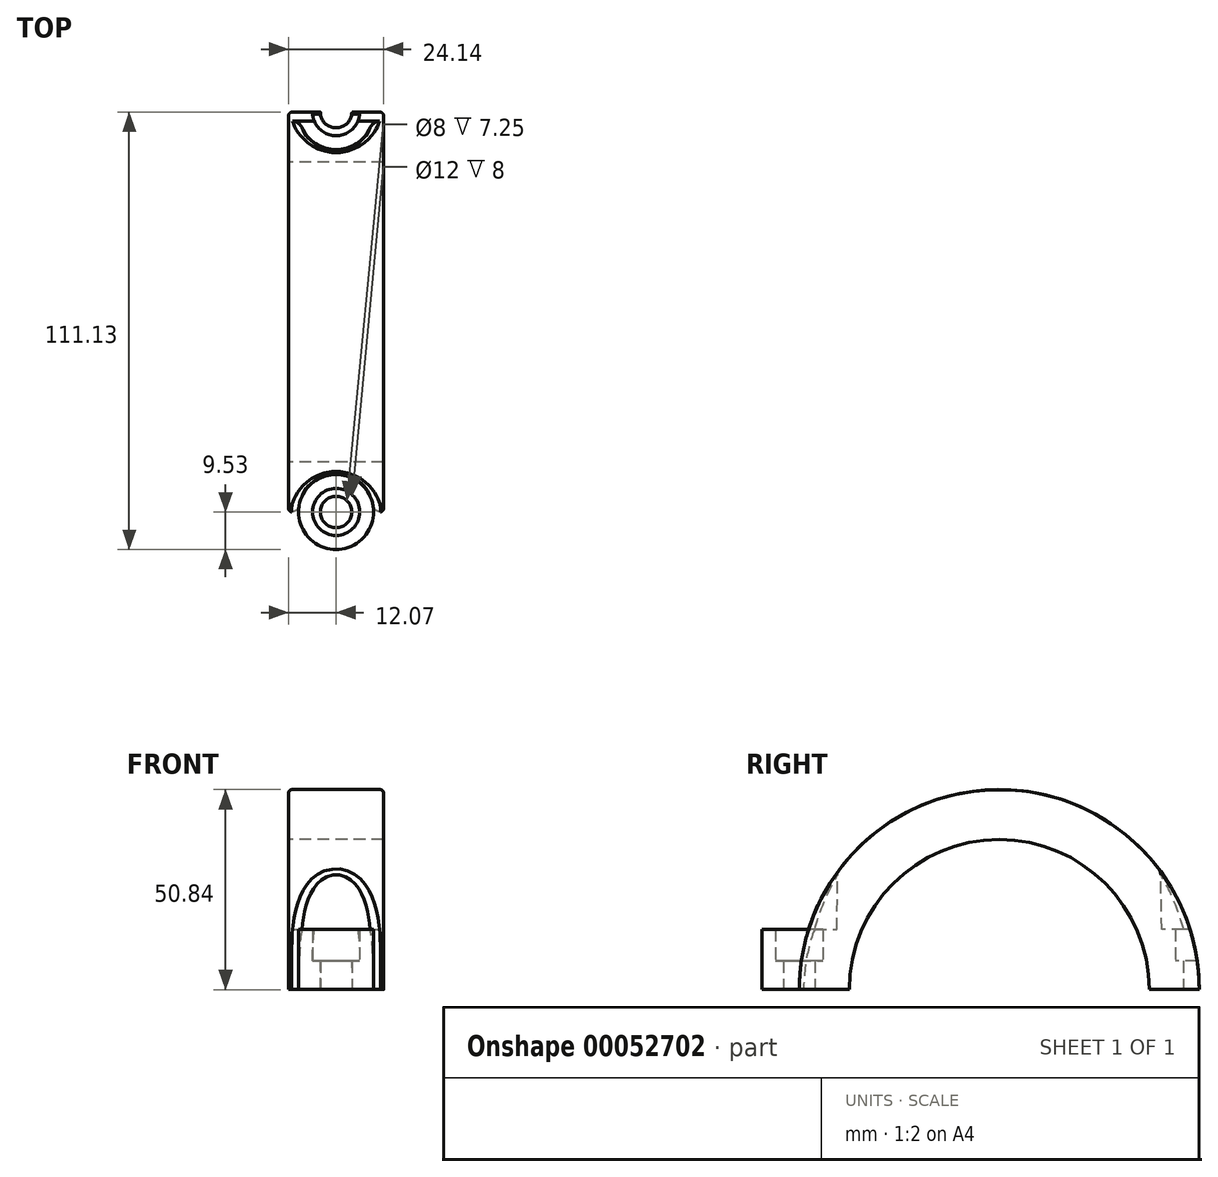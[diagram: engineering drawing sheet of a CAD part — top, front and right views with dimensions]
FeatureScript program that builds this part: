
annotation { "Feature Type Name" : "Feature", "Feature Type Description" : "" }
export const myFeature = defineFeature(function(context is Context, id is Id, definition is map)
    precondition{}
    {
        {
            var Q0;
            Q0=qCreatedBy(makeId("Right.planeOp"),FACE);
            var sketch = newSketch(context, id + "F0", { "sketchPlane" : qUnion([Q0])});
            skArc(sketch, "E0", {"start": v(38.1, 0) * mm, "mid": v(0, 38.1) * mm, "end": v(-38.1, 0) * mm});
            skArc(sketch, "E1.0", {"start": v(50.8, 0) * mm, "mid": v(0, 50.8) * mm, "end": v(-50.8, 0) * mm});
            skLineSegment(sketch, "E2", {"start": v(-50.8, 0) * mm, "end": v(-38.1, 0) * mm});
            skLineSegment(sketch, "E3.trimOffspring", {"start": v(38.1, 0) * mm, "end": v(50.8, 0) * mm});
            skSolve(sketch);
        }
        {
            var Q0;
            Q0 = qSketchRegion(id + "F0", true);
            var Q1;
            Q1=makeQuery(id+"F0.imprint","IMPRINT",FACE,{"disambiguationData":[TD([[makeQuery(id+"F0.imprint","IMPRINT",EDGE,{"derivedFrom":sQuery(id+"F0.wireOp",EDGE,"E0")}),-1.0]])]});
            extrude(context, id + "F1", {"entities" : qUnion([Q0, Q1]), "depth" : 24.13 * mm, "symmetric" : true});
        }
        {
            var Q0;
            Q0=makeQuery(id+"F1.opExtrude","SWEPT_FACE",FACE,{"disambiguationData":[OSD([sQuery(id+"F0.wireOp",EDGE,"E2")])]});
            var sketch = newSketch(context, id + "F2", { "sketchPlane" : qUnion([Q0])});
            skCircle(sketch, "E4", {"center": v(0, 50.8) * mm, "radius": 9.53 * mm});
            skCircle(sketch, "E5.MirrorC", {"center": v(0, -50.8) * mm, "radius": 9.53 * mm});
            skSolve(sketch);
        }
        {
            var Q0;
            {var subQ0=sQuery(id+"F2.wireOp",EDGE,"E4");var subQ1=makeQuery(id+"F1.opExtrude","SWEPT_EDGE",EDGE,{"disambiguationData":[OSD([sQuery(id+"F0.wireOp",EDGE,"E1.0"),sQuery(id+"F0.wireOp",EDGE,"E2")])]});var subQ2=makeQuery(id+"F2.imprint","INTERSECT",VERTEX,{"disambiguationData":[OD(0.0)],"derivedFrom":[subQ1,subQ0]});Q0=makeQuery(id+"F2.imprint","IMPRINT",FACE,{"disambiguationData":[TD([[makeQuery(id+"F2.imprint","IMPRINT",EDGE,{"disambiguationData":[TD([[subQ2,-1.0]])],"derivedFrom":subQ0}),1.0]])]});}
            var Q1;
            {var subQ0=sQuery(id+"F2.wireOp",EDGE,"E4");var subQ1=makeQuery(id+"F1.opExtrude","SWEPT_EDGE",EDGE,{"disambiguationData":[OSD([sQuery(id+"F0.wireOp",EDGE,"E1.0"),sQuery(id+"F0.wireOp",EDGE,"E2")])]});var subQ2=makeQuery(id+"F2.imprint","INTERSECT",VERTEX,{"disambiguationData":[OD(0.0)],"derivedFrom":[subQ1,subQ0]});Q1=makeQuery(id+"F2.imprint","IMPRINT",FACE,{"disambiguationData":[TD([[makeQuery(id+"F2.imprint","IMPRINT",EDGE,{"disambiguationData":[TD([[subQ2,1.0]])],"derivedFrom":subQ0}),1.0]])]});}
            var Q2;
            Q2=makeQuery(id+"F2.imprint","IMPRINT",FACE,{"disambiguationData":[TD([[makeQuery(id+"F2.imprint","IMPRINT",EDGE,{"derivedFrom":sQuery(id+"F2.wireOp",EDGE,"E5.MirrorC")}),-1.0]])]});
            extrude(context, id + "F3", {"entities" : qUnion([Q0, Q1, Q2]), "operationType" : NewBodyOperationType.ADD, "oppositeDirection" : true, "depth" : 15.25 * mm});
        }
        {
            var Q0;
            Q0=makeQuery(id+"F3.opExtrude","CAP_FACE",FACE,{"disambiguationData":[OSD([sQuery(id+"F2.wireOp",EDGE,"E4")])],"isStart":false});
            var sketch = newSketch(context, id + "F4", { "sketchPlane" : qUnion([Q0])});
            skCircle(sketch, "E6.MirrorC", {"center": v(0, 50.8) * mm, "radius": 9.53 * mm});
            skCircle(sketch, "E7.MirrorC", {"center": v(0, -50.8) * mm, "radius": 9.53 * mm});
            skSolve(sketch);
        }
        {
            var Q0;
            Q0 = qSketchRegion(id + "F4", true);
            extrude(context, id + "F5", {"entities" : qUnion([Q0]), "operationType" : NewBodyOperationType.REMOVE, "depth" : 15.25 * mm, "hasDraft" : true, "draftAngle" : 1 * degree});
        }
        {
            var Q0;
            Q0=sQuery(id+"F4.wireOp",VERTEX,"E6.MirrorC.center");
            var Q1;
            Q1=sQuery(id+"F4.wireOp",VERTEX,"E7.MirrorC.center");
            var Q2;
            Q2=makeQuery(id+"F1.opExtrude","SWEPT_BODY",BODY,{"disambiguationData":[OSD([sQuery(id+"F0.wireOp",EDGE,"E0"),sQuery(id+"F0.wireOp",EDGE,"E1.0"),sQuery(id+"F0.wireOp",EDGE,"E2"),sQuery(id+"F0.wireOp",EDGE,"E3.trimOffspring")])]});
            hole(context, id + "F6", {"style" : HoleStyle.C_BORE, "holeDiameter" : 8 * mm, "cBoreDiameter" : 12 * mm, "cBoreDepth" : 8 * mm, "endStyle" : HoleEndStyle.THROUGH, "locations" : qUnion([Q0, Q1]), "scope" : qUnion([Q2])});
        }
        {
            var Q0;
            Q0=makeQuery(id+"F1.opExtrude","CAP_EDGE",EDGE,{"disambiguationData":[OSD([sQuery(id+"F0.wireOp",EDGE,"E1.0")])],"isStart":false});
            var Q1;
            Q1=makeQuery(id+"F1.opExtrude","CAP_EDGE",EDGE,{"disambiguationData":[OSD([sQuery(id+"F0.wireOp",EDGE,"E1.0")])],"isStart":true});
            fillet(context, id + "F7", {"entities" : qUnion([Q0, Q1]), "radius" : 0.9 * mm, "tangentPropagation" : true, "allowEdgeOverflow" : false});
        }
        {
            var Q0;
            Q0=makeQuery(id+"F5.boolean.opBoolean","INTERSECT",EDGE,{"derivedFrom":[makeQuery(id+"F1.opExtrude","SWEPT_FACE",FACE,{"disambiguationData":[OSD([sQuery(id+"F0.wireOp",EDGE,"E1.0")])]}),makeQuery(id+"F5.opExtrude","SWEPT_FACE",FACE,{"disambiguationData":[OSD([sQuery(id+"F4.wireOp",EDGE,"E7.MirrorC")])]})]});
            var Q1;
            Q1=makeQuery(id+"F5.boolean.opBoolean","INTERSECT",EDGE,{"derivedFrom":[makeQuery(id+"F1.opExtrude","SWEPT_FACE",FACE,{"disambiguationData":[OSD([sQuery(id+"F0.wireOp",EDGE,"E1.0")])]}),makeQuery(id+"F5.opExtrude","SWEPT_FACE",FACE,{"disambiguationData":[OSD([sQuery(id+"F4.wireOp",EDGE,"E6.MirrorC")])]})]});
            fillet(context, id + "F8", {"entities" : qUnion([Q0, Q1]), "radius" : 2.54 * mm, "tangentPropagation" : true, "allowEdgeOverflow" : false});
        }
    });
